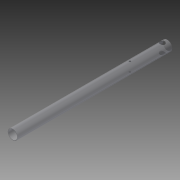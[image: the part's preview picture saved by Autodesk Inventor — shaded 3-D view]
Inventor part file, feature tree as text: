
AUTODESK INVENTOR PART (.ipt)
format: ipt  version: 2014 SP1 (Build 180222100, 222)  size: 100,864 bytes
history: native  units: in
note: dims shown in document units (in); Inventor stores cm internally (conversion verified against a paired STEP export)
features: extrude x2, sketch x2, plane x1
ambient origin geometry x8: Origin, YZ Plane, XZ Plane, XY Plane, X Axis, Y Axis, Z Axis, Center Point
bodies: Solid1 (feature_tree)
feature tree (5):
  extrude  "Extrusion1"  Depth=0.875in
  plane  "Work Plane1"
  extrude  "Extrusion2"  Depth=0.5in
  sketch  "Sketch1"  dims[d0=1.0in d1=0.875in]
  sketch  "Sketch2"  dims[d2=15.5in d3=0.0in d4=0.5in d6=0.5in d8=1.0in d9=0.0in d10=0.19in d11=3.75in]
